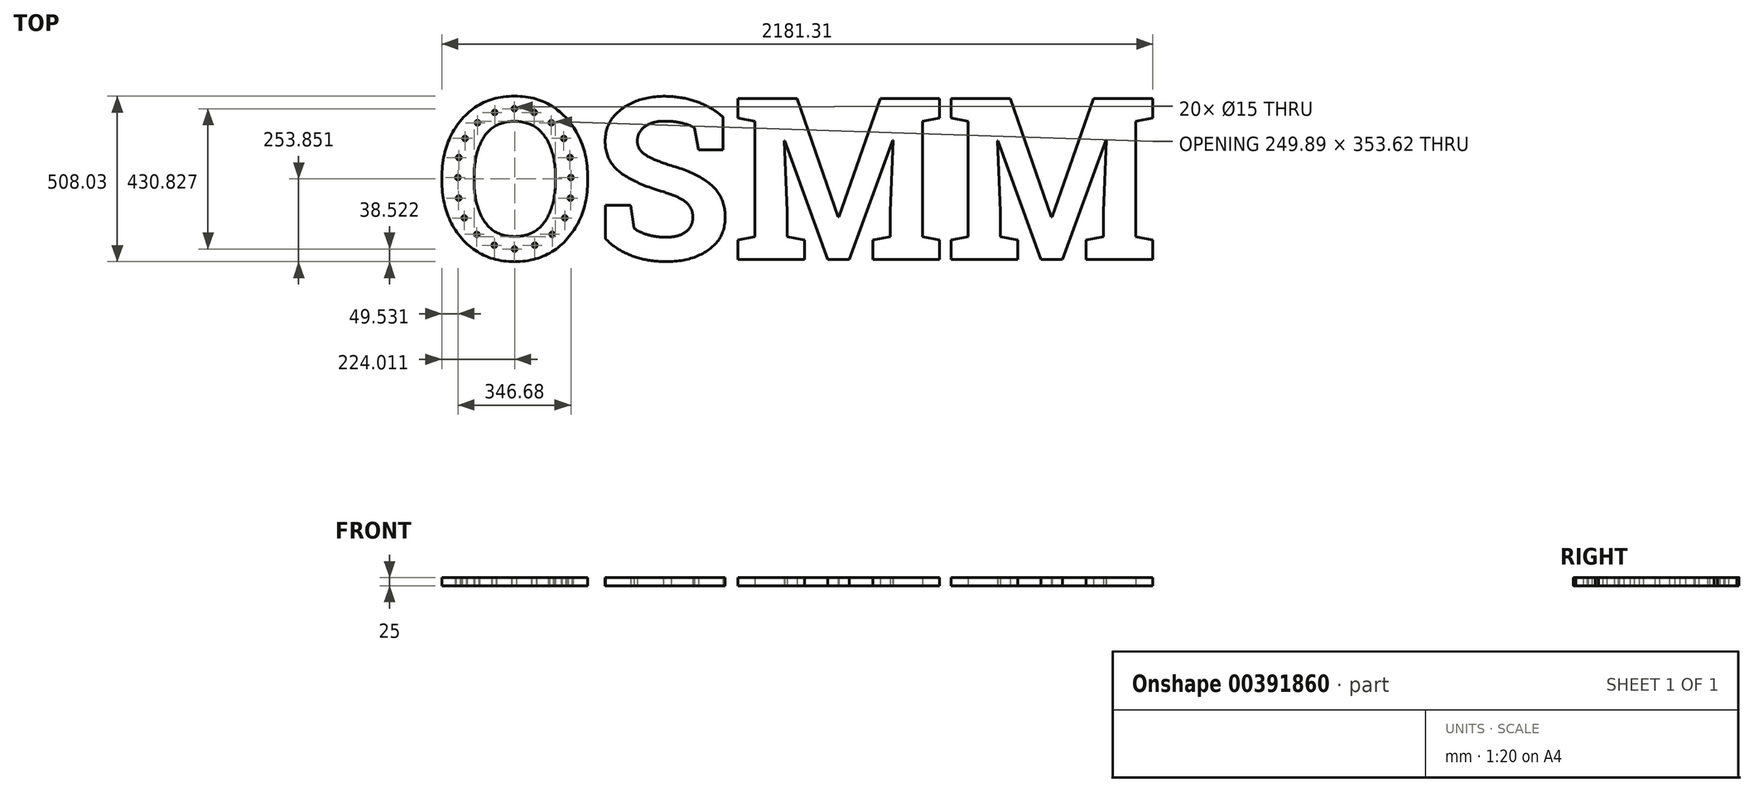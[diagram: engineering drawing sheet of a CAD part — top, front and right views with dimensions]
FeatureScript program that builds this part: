
annotation { "Feature Type Name" : "Feature", "Feature Type Description" : "" }
export const myFeature = defineFeature(function(context is Context, id is Id, definition is map)
    precondition{}
    {
        {
            var Q0;
            Q0=qCreatedBy(makeId("Top.planeOp"),FACE);
            var sketch = newSketch(context, id + "F0", { "sketchPlane" : qUnion([Q0])});
            skText(sketch, "E0", { "text": "OSMM", "fontName": "RobotoSlab-Bold.ttf"});
            const initialGuessF0  = {"E0": [-1.17865, -0.24529, 1, 0, 0.5]};
            skSetInitialGuess(sketch, initialGuessF0);
            skSolve(sketch);
        }
        {
            var Q0;
            Q0=makeQuery(id+"F0.imprint","IMPRINT",FACE,{"disambiguationData":[TD([[makeQuery(id+"F0.imprint","IMPRINT",EDGE,{"derivedFrom":sQuery(id+"F0.wireOp",EDGE,"E0.sketch_text.stroke-0")}),-1.0]])]});
            var Q1;
            Q1=makeQuery(id+"F0.imprint","IMPRINT",FACE,{"disambiguationData":[TD([[makeQuery(id+"F0.imprint","IMPRINT",EDGE,{"derivedFrom":sQuery(id+"F0.wireOp",EDGE,"E0.sketch_text.stroke-20")}),-1.0]])]});
            var Q2;
            Q2=makeQuery(id+"F0.imprint","IMPRINT",FACE,{"disambiguationData":[TD([[makeQuery(id+"F0.imprint","IMPRINT",EDGE,{"derivedFrom":sQuery(id+"F0.wireOp",EDGE,"E0.sketch_text.stroke-50")}),-1.0]])]});
            var Q3;
            Q3=makeQuery(id+"F0.imprint","IMPRINT",FACE,{"disambiguationData":[TD([[makeQuery(id+"F0.imprint","IMPRINT",EDGE,{"derivedFrom":sQuery(id+"F0.wireOp",EDGE,"E0.sketch_text.stroke-81")}),-1.0]])]});
            extrude(context, id + "F1", {"entities" : qUnion([Q0, Q1, Q2, Q3]), "depth" : 25 * mm});
        }
        {
            var Q0;
            Q0=makeQuery(id+"F1.opExtrude","CAP_FACE",FACE,{"disambiguationData":[OSD([sQuery(id+"F0.wireOp",EDGE,"E0.sketch_text.stroke-0"),sQuery(id+"F0.wireOp",EDGE,"E0.sketch_text.stroke-1"),sQuery(id+"F0.wireOp",EDGE,"E0.sketch_text.stroke-2"),sQuery(id+"F0.wireOp",EDGE,"E0.sketch_text.stroke-3"),sQuery(id+"F0.wireOp",EDGE,"E0.sketch_text.stroke-4"),sQuery(id+"F0.wireOp",EDGE,"E0.sketch_text.stroke-5"),sQuery(id+"F0.wireOp",EDGE,"E0.sketch_text.stroke-6"),sQuery(id+"F0.wireOp",EDGE,"E0.sketch_text.stroke-7"),sQuery(id+"F0.wireOp",EDGE,"E0.sketch_text.stroke-8"),sQuery(id+"F0.wireOp",EDGE,"E0.sketch_text.stroke-9"),sQuery(id+"F0.wireOp",EDGE,"E0.sketch_text.stroke-10"),sQuery(id+"F0.wireOp",EDGE,"E0.sketch_text.stroke-11"),sQuery(id+"F0.wireOp",EDGE,"E0.sketch_text.stroke-12"),sQuery(id+"F0.wireOp",EDGE,"E0.sketch_text.stroke-13"),sQuery(id+"F0.wireOp",EDGE,"E0.sketch_text.stroke-14"),sQuery(id+"F0.wireOp",EDGE,"E0.sketch_text.stroke-15"),sQuery(id+"F0.wireOp",EDGE,"E0.sketch_text.stroke-16"),sQuery(id+"F0.wireOp",EDGE,"E0.sketch_text.stroke-17"),sQuery(id+"F0.wireOp",EDGE,"E0.sketch_text.stroke-18"),sQuery(id+"F0.wireOp",EDGE,"E0.sketch_text.stroke-19")])],"isStart":false});
            var sketch = newSketch(context, id + "F2", { "sketchPlane" : qUnion([Q0])});
            skArc(sketch, "E1", {"start": v(-1104.9, 53.98) * mm, "mid": v(-1106.45, 1.49) * mm, "end": v(-1104.9, -51) * mm, "construction": true});
            skArc(sketch, "E2", {"start": v(-759.24, 53.98) * mm, "mid": v(-932.07, 216.9) * mm, "end": v(-1104.9, 53.98) * mm, "construction": true});
            skArc(sketch, "E3", {"start": v(-759.24, -51) * mm, "mid": v(-757.69, 1.49) * mm, "end": v(-759.24, 53.98) * mm, "construction": true});
            skArc(sketch, "E4", {"start": v(-1104.9, -51) * mm, "mid": v(-932.07, -213.93) * mm, "end": v(-759.24, -51) * mm, "construction": true});
            skLineSegment(sketch, "E5", {"start": v(-1104.9, -51) * mm, "end": v(-759.24, -51) * mm, "construction": true});
            skLineSegment(sketch, "E6", {"start": v(-1104.9, 53.98) * mm, "end": v(-759.24, 53.98) * mm, "construction": true});
            skLineSegment(sketch, "E7", {"start": v(-1056.9, 6.02) * mm, "end": v(-1155.97, 5.26) * mm, "construction": true});
            skPoint(sketch, "E8", {"position": v(-1106.44, 5.64) * mm});
            skLineSegment(sketch, "E9", {"start": v(-807.01, 6.02) * mm, "end": v(-708.38, 5.26) * mm, "construction": true});
            skPoint(sketch, "E10", {"position": v(-757.7, 5.64) * mm});
            skLineSegment(sketch, "E11", {"start": v(-932.77, -175.4) * mm, "end": v(-932.77, -252.45) * mm, "construction": true});
            skPoint(sketch, "E12", {"position": v(-932.77, -213.93) * mm});
            skLineSegment(sketch, "E13", {"start": v(-933.1, 178.22) * mm, "end": v(-933.1, 255.58) * mm, "construction": true});
            skPoint(sketch, "E14", {"position": v(-933.1, 216.9) * mm});
            skCircle(sketch, "E15", {"center": v(-1106.44, 5.64) * mm, "radius": 7.5 * mm});
            skCircle(sketch, "E16", {"center": v(-933.1, 216.9) * mm, "radius": 7.5 * mm});
            skCircle(sketch, "E17", {"center": v(-1046.33, 173.85) * mm, "radius": 7.5 * mm});
            skCircle(sketch, "E18", {"center": v(-1084.61, 125.66) * mm, "radius": 7.5 * mm});
            skCircle(sketch, "E19", {"center": v(-1103.62, 67.12) * mm, "radius": 7.5 * mm});
            skCircle(sketch, "E20", {"center": v(-993.6, 205.6) * mm, "radius": 7.5 * mm});
            skLineSegment(sketch, "E21", {"start": v(-1106.44, 5.64) * mm, "end": v(-1103.62, 67.12) * mm, "construction": true});
            skLineSegment(sketch, "E22", {"start": v(-1084.61, 125.66) * mm, "end": v(-1103.62, 67.12) * mm, "construction": true});
            skLineSegment(sketch, "E23", {"start": v(-1046.33, 173.85) * mm, "end": v(-1084.61, 125.66) * mm, "construction": true});
            skLineSegment(sketch, "E24", {"start": v(-993.6, 205.6) * mm, "end": v(-1046.33, 173.85) * mm, "construction": true});
            skLineSegment(sketch, "E25", {"start": v(-933.1, 216.9) * mm, "end": v(-993.6, 205.6) * mm, "construction": true});
            skCircle(sketch, "E26.MirrorC", {"center": v(-872.6, 205.6) * mm, "radius": 7.5 * mm});
            skCircle(sketch, "E27.MirrorC", {"center": v(-819.87, 173.85) * mm, "radius": 7.5 * mm});
            skCircle(sketch, "E28.MirrorC", {"center": v(-781.59, 125.66) * mm, "radius": 7.5 * mm});
            skCircle(sketch, "E29.MirrorC", {"center": v(-762.58, 67.12) * mm, "radius": 7.5 * mm});
            skCircle(sketch, "E30.MirrorC", {"center": v(-759.76, 5.64) * mm, "radius": 7.5 * mm});
            skCircle(sketch, "E31", {"center": v(-1104.38, -57.58) * mm, "radius": 7.5 * mm});
            skCircle(sketch, "E32", {"center": v(-1086.86, -118.36) * mm, "radius": 7.5 * mm});
            skCircle(sketch, "E33", {"center": v(-1048.67, -168.78) * mm, "radius": 7.5 * mm});
            skCircle(sketch, "E34", {"center": v(-994.91, -202.12) * mm, "radius": 7.5 * mm});
            skCircle(sketch, "E35", {"center": v(-932.77, -213.93) * mm, "radius": 7.5 * mm});
            skLineSegment(sketch, "E36", {"start": v(-1106.44, 5.64) * mm, "end": v(-1104.38, -57.58) * mm, "construction": true});
            skLineSegment(sketch, "E37", {"start": v(-1104.38, -57.58) * mm, "end": v(-1086.86, -118.36) * mm, "construction": true});
            skLineSegment(sketch, "E38", {"start": v(-1086.86, -118.36) * mm, "end": v(-1048.67, -168.78) * mm, "construction": true});
            skLineSegment(sketch, "E39", {"start": v(-1048.67, -168.78) * mm, "end": v(-994.91, -202.12) * mm, "construction": true});
            skLineSegment(sketch, "E40", {"start": v(-994.91, -202.12) * mm, "end": v(-932.77, -213.93) * mm, "construction": true});
            skLineSegment(sketch, "E41.MirrorCS", {"start": v(-932.45, 216.9) * mm, "end": v(-871.95, 205.6) * mm, "construction": true});
            skLineSegment(sketch, "E42.MirrorCS", {"start": v(-871.95, 205.6) * mm, "end": v(-819.22, 173.85) * mm, "construction": true});
            skLineSegment(sketch, "E43.MirrorCS", {"start": v(-819.22, 173.85) * mm, "end": v(-780.94, 125.66) * mm, "construction": true});
            skLineSegment(sketch, "E44.MirrorCS", {"start": v(-759.1, 5.64) * mm, "end": v(-761.93, 67.12) * mm, "construction": true});
            skLineSegment(sketch, "E45.MirrorCS", {"start": v(-780.94, 125.66) * mm, "end": v(-761.93, 67.12) * mm, "construction": true});
            skCircle(sketch, "E46.MirrorC", {"center": v(-870.63, -202.12) * mm, "radius": 7.5 * mm});
            skCircle(sketch, "E47.MirrorC", {"center": v(-816.88, -168.78) * mm, "radius": 7.5 * mm});
            skCircle(sketch, "E48.MirrorC", {"center": v(-778.7, -118.36) * mm, "radius": 7.5 * mm});
            skCircle(sketch, "E49.MirrorC", {"center": v(-761.16, -57.58) * mm, "radius": 7.5 * mm});
            skSolve(sketch);
        }
        {
            var Q0;
            Q0 = qSketchRegion(id + "F2", true);
            extrude(context, id + "F3", {"entities" : qUnion([Q0]), "operationType" : NewBodyOperationType.REMOVE, "endBound" : BoundingType.THROUGH_ALL, "oppositeDirection" : true, "depth" : 25 * mm});
        }
    });
